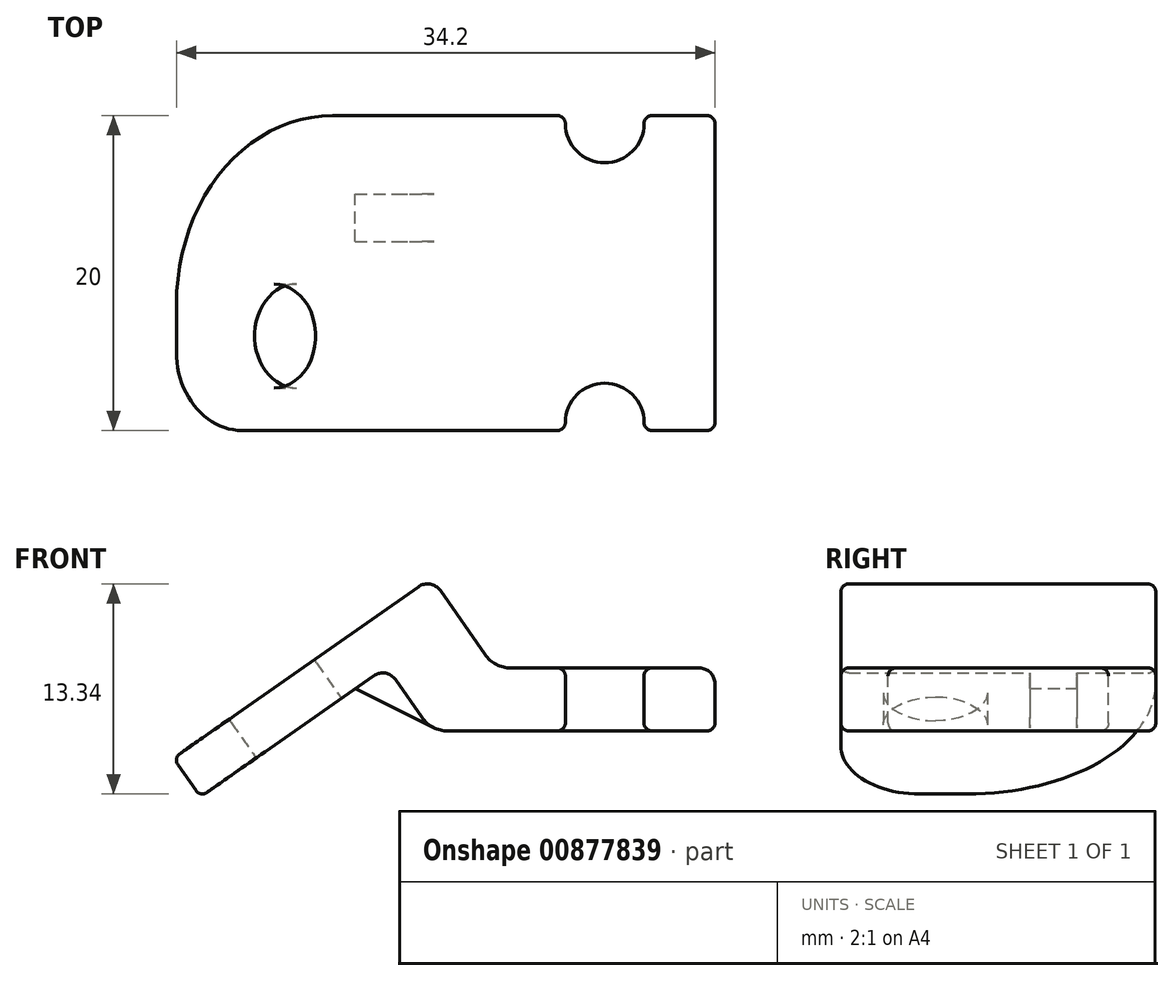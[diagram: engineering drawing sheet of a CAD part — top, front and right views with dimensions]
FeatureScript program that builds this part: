
annotation { "Feature Type Name" : "Feature", "Feature Type Description" : "" }
export const myFeature = defineFeature(function(context is Context, id is Id, definition is map)
    precondition{}
    {
        {
            var Q0;
            Q0=qCreatedBy(makeId("Front.planeOp"),FACE);
            var sketch = newSketch(context, id + "F0", { "sketchPlane" : qUnion([Q0])});
            skLineSegment(sketch, "E0", {"start": v(-18, 0) * mm, "end": v(0, 0) * mm});
            skLineSegment(sketch, "E1", {"start": v(0, 0) * mm, "end": v(0, 4) * mm});
            skLineSegment(sketch, "E2", {"start": v(0, 4) * mm, "end": v(-14, 4) * mm});
            skLineSegment(sketch, "E3", {"start": v(-14, 4) * mm, "end": v(-18.02, 9.73) * mm});
            skLineSegment(sketch, "E4", {"start": v(-18.02, 9.73) * mm, "end": v(-34.4, -1.74) * mm});
            skLineSegment(sketch, "E5", {"start": v(-34.4, -1.74) * mm, "end": v(-32.68, -4.2) * mm});
            skLineSegment(sketch, "E6", {"start": v(-32.68, -4.2) * mm, "end": v(-20.86, 4.08) * mm});
            skLineSegment(sketch, "E7", {"start": v(-18, 0) * mm, "end": v(-20.86, 4.08) * mm});
            skSolve(sketch);
        }
        {
            var Q0;
            Q0=qSketchRegion(id+"F0",true);
            extrude(context, id + "F1", {"entities" : qUnion([Q0]), "depth" : 20 * mm});
        }
        {
            var Q0;
            Q0=makeQuery(id+"F1.opExtrude","SWEPT_FACE",FACE,{"disambiguationData":[OSD([sQuery(id+"F0.wireOp",EDGE,"E2")])]});
            var sketch = newSketch(context, id + "F2", { "sketchPlane" : qUnion([Q0])});
            skCircle(sketch, "E8", {"center": v(-7, -0.5) * mm, "radius": 2.5 * mm});
            skCircle(sketch, "E9", {"center": v(-7, -19.5) * mm, "radius": 2.5 * mm});
            skLineSegment(sketch, "E10", {"start": v(-14, -10) * mm, "end": v(0, -10) * mm, "construction": true});
            skLineSegment(sketch, "E11", {"start": v(-7, -10) * mm, "end": v(-7, -0.5) * mm, "construction": true});
            skLineSegment(sketch, "E12", {"start": v(-7, -10) * mm, "end": v(-7, -19.5) * mm, "construction": true});
            skSolve(sketch);
        }
        {
            var Q0;
            Q0=qSketchRegion(id+"F2",true);
            extrude(context, id + "F3", {"entities" : qUnion([Q0]), "operationType" : NewBodyOperationType.REMOVE, "endBound" : BoundingType.THROUGH_ALL, "oppositeDirection" : true, "depth" : 25.4 * mm});
        }
        {
            var Q0;
            Q0=makeQuery(id+"F1.opExtrude","SWEPT_EDGE",EDGE,{"disambiguationData":[OSD([sQuery(id+"F0.wireOp",EDGE,"E6"),sQuery(id+"F0.wireOp",EDGE,"E7")])]});
            fillet(context, id + "F4", {"entities" : qUnion([Q0]), "radius" : 1 * mm, "tangentPropagation" : true, "allowEdgeOverflow" : false});
        }
        {
            var Q0;
            Q0=makeQuery(id+"F1.opExtrude","SWEPT_FACE",FACE,{"disambiguationData":[OSD([sQuery(id+"F0.wireOp",EDGE,"E6")])]});
            var sketch = newSketch(context, id + "F5", { "sketchPlane" : qUnion([Q0])});
            skLineSegment(sketch, "E13", {"start": v(-15.74, 14) * mm, "end": v(-29.17, 14) * mm, "construction": true});
            skCircle(sketch, "E14", {"center": v(-21.55, 14) * mm, "radius": 3.3 * mm});
            skSolve(sketch);
        }
        {
            var Q0;
            Q0=qSketchRegion(id+"F5",true);
            extrude(context, id + "F6", {"entities" : qUnion([Q0]), "operationType" : NewBodyOperationType.REMOVE, "endBound" : BoundingType.THROUGH_ALL, "oppositeDirection" : true, "depth" : 25.4 * mm});
        }
        {
            var Q0;
            Q0=makeQuery(id+"F1.opExtrude","CAP_EDGE",EDGE,{"disambiguationData":[OSD([sQuery(id+"F0.wireOp",EDGE,"E5")])],"isStart":true});
            fillet(context, id + "F7", {"entities" : qUnion([Q0]), "radius" : 12 * mm, "tangentPropagation" : true, "allowEdgeOverflow" : false});
        }
        {
            var Q0;
            Q0=makeQuery(id+"F1.opExtrude","CAP_EDGE",EDGE,{"disambiguationData":[OSD([sQuery(id+"F0.wireOp",EDGE,"E5")])],"isStart":false});
            fillet(context, id + "F8", {"entities" : qUnion([Q0]), "radius" : 5 * mm, "tangentPropagation" : true, "allowEdgeOverflow" : false});
        }
        {
            var Q0;
            Q0=makeQuery(id+"F1.opExtrude","SWEPT_EDGE",EDGE,{"disambiguationData":[OSD([sQuery(id+"F0.wireOp",EDGE,"E3"),sQuery(id+"F0.wireOp",EDGE,"E4")])]});
            fillet(context, id + "F9", {"entities" : qUnion([Q0]), "radius" : 1 * mm, "tangentPropagation" : true, "allowEdgeOverflow" : false});
        }
        {
            var Q0;
            Q0=makeQuery(id+"F1.opExtrude","SWEPT_EDGE",EDGE,{"disambiguationData":[OSD([sQuery(id+"F0.wireOp",EDGE,"E2"),sQuery(id+"F0.wireOp",EDGE,"E3")])]});
            fillet(context, id + "F10", {"entities" : qUnion([Q0]), "radius" : 2 * mm, "tangentPropagation" : true, "allowEdgeOverflow" : false});
        }
        {
            var Q0;
            Q0=makeQuery(id+"F1.opExtrude","SWEPT_EDGE",EDGE,{"disambiguationData":[OSD([sQuery(id+"F0.wireOp",EDGE,"E0"),sQuery(id+"F0.wireOp",EDGE,"E7")])]});
            fillet(context, id + "F11", {"entities" : qUnion([Q0]), "radius" : 2 * mm, "tangentPropagation" : true, "allowEdgeOverflow" : false});
        }
        {
            var Q0;
            Q0=makeQuery(id+"F1.opExtrude","SWEPT_EDGE",EDGE,{"disambiguationData":[OSD([sQuery(id+"F0.wireOp",EDGE,"E1"),sQuery(id+"F0.wireOp",EDGE,"E2")])]});
            fillet(context, id + "F12", {"entities" : qUnion([Q0]), "radius" : 1 * mm, "tangentPropagation" : true, "allowEdgeOverflow" : false});
        }
        {
            var Q0;
            {var subQ0=sQuery(id+"F0.wireOp",EDGE,"E4");var subQ1=sQuery(id+"F0.wireOp",EDGE,"E2");var subQ2=sQuery(id+"F0.wireOp",EDGE,"E3");var subQ3=sQuery(id+"F0.wireOp",EDGE,"E0");var subQ4=sQuery(id+"F0.wireOp",EDGE,"E5");var subQ5=sQuery(id+"F0.wireOp",EDGE,"E6");var subQ6=sQuery(id+"F0.wireOp",EDGE,"E7");Q0=makeQuery(id+"F3.boolean.opBoolean","SPLIT",FACE,{"disambiguationData":[TD([makeQuery(id+"F1.opExtrude","SWEPT_FACE",FACE,{"disambiguationData":[OSD([subQ2])]})])],"derivedFrom":makeQuery(id+"F1.opExtrude","CAP_FACE",FACE,{"disambiguationData":[OSD([subQ3,sQuery(id+"F0.wireOp",EDGE,"E1"),subQ1,subQ2,subQ0,subQ4,subQ5,subQ6])],"isStart":true})});}
            var Q1;
            {var subQ0=sQuery(id+"F0.wireOp",EDGE,"E0");var subQ1=sQuery(id+"F0.wireOp",EDGE,"E1");var subQ2=sQuery(id+"F0.wireOp",EDGE,"E2");Q1=makeQuery(id+"F3.boolean.opBoolean","SPLIT",FACE,{"disambiguationData":[TD([makeQuery(id+"F1.opExtrude","SWEPT_FACE",FACE,{"disambiguationData":[OSD([subQ1])]})])],"derivedFrom":makeQuery(id+"F1.opExtrude","CAP_FACE",FACE,{"disambiguationData":[OSD([subQ0,subQ1,subQ2,sQuery(id+"F0.wireOp",EDGE,"E3"),sQuery(id+"F0.wireOp",EDGE,"E4"),sQuery(id+"F0.wireOp",EDGE,"E5"),sQuery(id+"F0.wireOp",EDGE,"E6"),sQuery(id+"F0.wireOp",EDGE,"E7")])],"isStart":true})});}
            var Q2;
            Q2=makeQuery(id+"F7.opFillet","BLEND_FACE",FACE,{"disambiguationData":[OSD([sQuery(id+"F0.wireOp",EDGE,"E5")])]});
            var Q3;
            Q3=makeQuery(id+"F1.opExtrude","SWEPT_FACE",FACE,{"disambiguationData":[OSD([sQuery(id+"F0.wireOp",EDGE,"E5")])]});
            var Q4;
            Q4=makeQuery(id+"F8.opFillet","BLEND_FACE",FACE,{"disambiguationData":[OSD([sQuery(id+"F0.wireOp",EDGE,"E5")])]});
            var Q5;
            {var subQ0=sQuery(id+"F0.wireOp",EDGE,"E4");var subQ1=sQuery(id+"F0.wireOp",EDGE,"E2");var subQ2=sQuery(id+"F0.wireOp",EDGE,"E3");var subQ3=sQuery(id+"F0.wireOp",EDGE,"E0");var subQ4=sQuery(id+"F0.wireOp",EDGE,"E5");var subQ5=sQuery(id+"F0.wireOp",EDGE,"E6");var subQ6=sQuery(id+"F0.wireOp",EDGE,"E7");Q5=makeQuery(id+"F3.boolean.opBoolean","SPLIT",FACE,{"disambiguationData":[TD([makeQuery(id+"F1.opExtrude","SWEPT_FACE",FACE,{"disambiguationData":[OSD([subQ2])]})])],"derivedFrom":makeQuery(id+"F1.opExtrude","CAP_FACE",FACE,{"disambiguationData":[OSD([subQ3,sQuery(id+"F0.wireOp",EDGE,"E1"),subQ1,subQ2,subQ0,subQ4,subQ5,subQ6])],"isStart":false})});}
            var Q6;
            {var subQ0=sQuery(id+"F0.wireOp",EDGE,"E0");var subQ1=sQuery(id+"F0.wireOp",EDGE,"E1");var subQ2=sQuery(id+"F0.wireOp",EDGE,"E2");Q6=makeQuery(id+"F3.boolean.opBoolean","SPLIT",FACE,{"disambiguationData":[TD([makeQuery(id+"F1.opExtrude","SWEPT_FACE",FACE,{"disambiguationData":[OSD([subQ1])]})])],"derivedFrom":makeQuery(id+"F1.opExtrude","CAP_FACE",FACE,{"disambiguationData":[OSD([subQ0,subQ1,subQ2,sQuery(id+"F0.wireOp",EDGE,"E3"),sQuery(id+"F0.wireOp",EDGE,"E4"),sQuery(id+"F0.wireOp",EDGE,"E5"),sQuery(id+"F0.wireOp",EDGE,"E6"),sQuery(id+"F0.wireOp",EDGE,"E7")])],"isStart":false})});}
            var Q7;
            Q7=makeQuery(id+"F3.boolean.opBoolean","COPY",FACE,{"derivedFrom":makeQuery(id+"F3.opExtrude","SWEPT_FACE",FACE,{"disambiguationData":[OSD([sQuery(id+"F2.wireOp",EDGE,"E9")])]})});
            var Q8;
            Q8=makeQuery(id+"F3.boolean.opBoolean","COPY",FACE,{"derivedFrom":makeQuery(id+"F3.opExtrude","SWEPT_FACE",FACE,{"disambiguationData":[OSD([sQuery(id+"F2.wireOp",EDGE,"E8")])]})});
            var Q9;
            Q9=makeQuery(id+"F1.opExtrude","SWEPT_FACE",FACE,{"disambiguationData":[OSD([sQuery(id+"F0.wireOp",EDGE,"E1")])]});
            fillet(context, id + "F13", {"entities" : qUnion([Q0, Q1, Q2, Q3, Q4, Q5, Q6, Q7, Q8, Q9]), "radius" : .5 * mm, "tangentPropagation" : true, "allowEdgeOverflow" : false});
        }
        {
            var Q0;
            {var subQ0=sQuery(id+"F0.wireOp",EDGE,"E4");var subQ1=sQuery(id+"F0.wireOp",EDGE,"E2");var subQ2=sQuery(id+"F0.wireOp",EDGE,"E3");var subQ3=sQuery(id+"F0.wireOp",EDGE,"E0");var subQ4=sQuery(id+"F0.wireOp",EDGE,"E5");var subQ5=sQuery(id+"F0.wireOp",EDGE,"E6");var subQ6=sQuery(id+"F0.wireOp",EDGE,"E7");Q0=makeQuery(id+"F3.boolean.opBoolean","SPLIT",FACE,{"disambiguationData":[TD([makeQuery(id+"F1.opExtrude","SWEPT_FACE",FACE,{"disambiguationData":[OSD([subQ2])]})])],"derivedFrom":makeQuery(id+"F1.opExtrude","CAP_FACE",FACE,{"disambiguationData":[OSD([subQ3,sQuery(id+"F0.wireOp",EDGE,"E1"),subQ1,subQ2,subQ0,subQ4,subQ5,subQ6])],"isStart":true})});}
            cPlane(context, id + "F14", {"entities" : qUnion([Q0]), "cplaneType" : CPlaneType.OFFSET, "offset" : 5 * mm, "oppositeDirection" : true, "width" : 152.4 * mm, "height" : 152.4 * mm});
        }
        {
            var Q0;
            Q0=qCreatedBy(id+"F14.planeOp",FACE);
            var sketch = newSketch(context, id + "F15", { "sketchPlane" : qUnion([Q0])});
            skArc(sketch, "E15.0", {"start": v(18.6, 0.85) * mm, "mid": v(18.1, 0.36) * mm, "end": v(17.47, 0.07) * mm});
            skLineSegment(sketch, "E16.0", {"start": v(20.28, 3.26) * mm, "end": v(18.6, 0.85) * mm});
            skArc(sketch, "E17.0", {"start": v(21.68, 3.5) * mm, "mid": v(20.93, 3.67) * mm, "end": v(20.28, 3.26) * mm});
            skLineSegment(sketch, "E18.0", {"start": v(22.85, 2.69) * mm, "end": v(21.68, 3.5) * mm});
            skLineSegment(sketch, "E19", {"start": v(22.85, 2.69) * mm, "end": v(17.47, 0.02) * mm});
            skPoint(sketch, "E19.endSnap0", {"position": v(17.47, 0.07) * mm});
            skPoint(sketch, "E20.orphan", {"position": v(16.96, 0) * mm});
            skSolve(sketch);
        }
        {
            var Q0;
            Q0=qSketchRegion(id+"F15",true);
            extrude(context, id + "F16", {"entities" : qUnion([Q0]), "operationType" : NewBodyOperationType.ADD, "oppositeDirection" : true, "depth" : 3 * mm});
        }
        {
            var Q0;
            Q0=makeQuery(id+"F6.boolean.opBoolean","COPY",FACE,{"derivedFrom":makeQuery(id+"F6.opExtrude","SWEPT_FACE",FACE,{"disambiguationData":[OSD([sQuery(id+"F5.wireOp",EDGE,"E14")])]})});
            fillet(context, id + "F17", {"entities" : qUnion([Q0]), "radius" : .25 * mm, "tangentPropagation" : true, "allowEdgeOverflow" : false});
        }
    });
